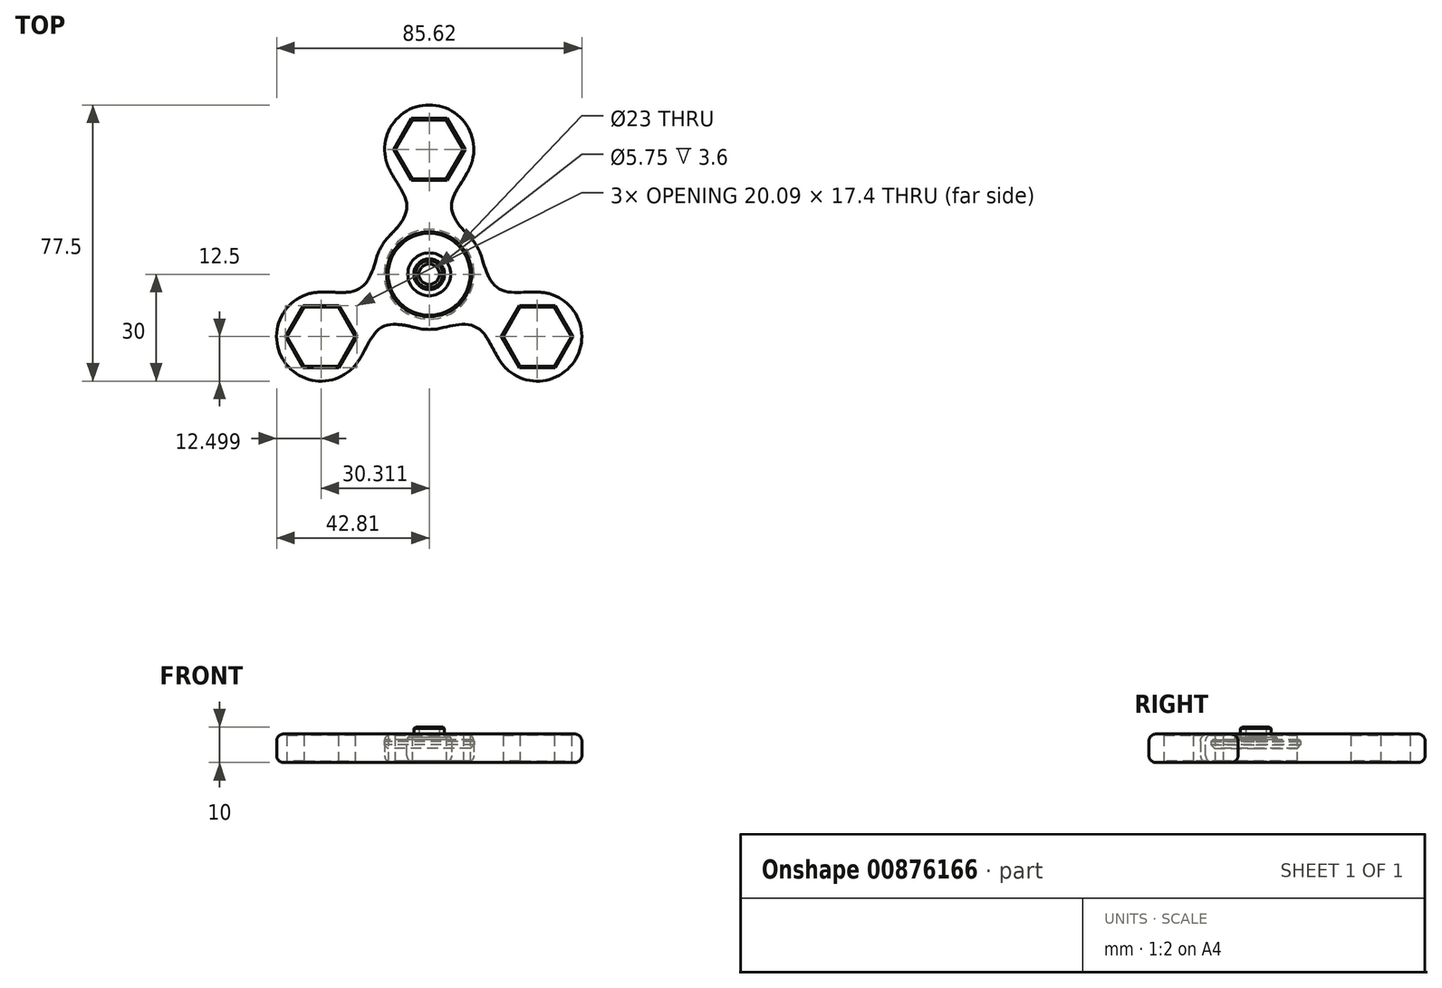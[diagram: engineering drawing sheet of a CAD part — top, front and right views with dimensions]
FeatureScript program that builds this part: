
annotation { "Feature Type Name" : "Feature", "Feature Type Description" : "" }
export const myFeature = defineFeature(function(context is Context, id is Id, definition is map)
    precondition{}
    {
        {
            var Q0;
            Q0=qCreatedBy(makeId("Top.planeOp"),FACE);
            var sketch = newSketch(context, id + "F0", { "sketchPlane" : qUnion([Q0])});
            skCircle(sketch, "E0", {"center": v(0, 0) * mm, "radius": 11.5 * mm});
            skLineSegment(sketch, "E1", {"start": v(0, 0) * mm, "end": v(0, 60.33) * mm, "construction": true});
            skLineSegment(sketch, "E2.1.0", {"start": v(0, 0) * mm, "end": v(-52.24, -30.16) * mm, "construction": true});
            skLineSegment(sketch, "E2.2.0", {"start": v(0, 0) * mm, "end": v(52.24, -30.16) * mm, "construction": true});
            skCircle(sketch, "E3", {"center": v(0, 0) * mm, "radius": 35 * mm, "construction": true});
            skCircle(sketch, "E4", {"center": v(0, 35) * mm, "radius": 12.5 * mm});
            skCircle(sketch, "E5.0", {"center": v(0, 0) * mm, "radius": 15.5 * mm});
            skFitSpline(sketch, "E6", {"points": [v(-12.1, 31.86) * mm, v(-6.42, 20.47) * mm, v(-10.95, 10.97) * mm], "startDerivative": vector(5.97, -22.99) * mm, "endDerivative": vector(-21.64, -21.6) * mm});
            skFitSpline(sketch, "E7.MirrorCS", {"points": [v(12.1, 31.86) * mm, v(6.42, 20.47) * mm, v(10.95, 10.97) * mm], "startDerivative": vector(-5.97, -22.99) * mm, "endDerivative": vector(21.64, -21.6) * mm});
            skCircle(sketch, "E8.cCircle", {"center": v(0, 35) * mm, "radius": 8.3 * mm, "construction": true});
            skLineSegment(sketch, "E8.0", {"start": v(4.8, 26.7) * mm, "end": v(-4.8, 26.7) * mm});
            skLineSegment(sketch, "E8.1", {"start": v(-4.8, 26.7) * mm, "end": v(-9.58, 35) * mm});
            skLineSegment(sketch, "E8.2", {"start": v(-9.58, 35) * mm, "end": v(-4.8, 43.3) * mm});
            skLineSegment(sketch, "E8.3", {"start": v(-4.8, 43.3) * mm, "end": v(4.8, 43.3) * mm});
            skLineSegment(sketch, "E8.4", {"start": v(4.8, 43.3) * mm, "end": v(9.58, 35) * mm});
            skLineSegment(sketch, "E8.5", {"start": v(9.58, 35) * mm, "end": v(4.8, 26.7) * mm});
            skPoint(sketch, "E8.0.midPoint", {"position": v(0, 26.7) * mm});
            skSolve(sketch);
        }
        {
            var Q0;
            Q0=makeQuery(id+"F0.imprint","IMPRINT",FACE,{"disambiguationData":[TD([[makeQuery(id+"F0.imprint","IMPRINT",EDGE,{"derivedFrom":sQuery(id+"F0.wireOp",EDGE,"E8.0")}),1.0]])]});
            var Q1;
            {var subQ0=sQuery(id+"F0.wireOp",EDGE,"E6");var subQ1=sQuery(id+"F0.wireOp",EDGE,"E4");var subQ2=makeQuery(id+"F0.imprint","INTERSECT",VERTEX,{"disambiguationData":[OD(1.0)],"derivedFrom":[subQ1,subQ0]});Q1=makeQuery(id+"F0.imprint","IMPRINT",FACE,{"disambiguationData":[TD([[makeQuery(id+"F0.imprint","IMPRINT",EDGE,{"disambiguationData":[TD([[subQ2,-1.0]])],"derivedFrom":subQ1}),-1.0]])]});}
            extrude(context, id + "F1", {"entities" : qUnion([Q0, Q1]), "endBound" : BoundingType.SYMMETRIC, "depth" : 8 * mm, "offsetDistance" : 25 * mm});
        }
        {
            var Q0;
            Q0=qCreatedBy(makeId("Front.planeOp"),FACE);
            var sketch = newSketch(context, id + "F2", { "sketchPlane" : qUnion([Q0])});
            skLineSegment(sketch, "E9", {"start": v(0, -33.65) * mm, "end": v(0, 33.2) * mm, "construction": true});
            skSolve(sketch);
        }
        {
            var Q0;
            Q0=makeQuery(id+"F1.opExtrude","SWEPT_BODY",BODY,{"disambiguationData":[OSD([sQuery(id+"F0.wireOp",EDGE,"E4"),sQuery(id+"F0.wireOp",EDGE,"E5.0"),sQuery(id+"F0.wireOp",EDGE,"E6"),sQuery(id+"F0.wireOp",EDGE,"E7.MirrorCS"),sQuery(id+"F0.wireOp",EDGE,"E8.0"),sQuery(id+"F0.wireOp",EDGE,"E8.1"),sQuery(id+"F0.wireOp",EDGE,"E8.2"),sQuery(id+"F0.wireOp",EDGE,"E8.3"),sQuery(id+"F0.wireOp",EDGE,"E8.4"),sQuery(id+"F0.wireOp",EDGE,"E8.5")])]});
            var Q1;
            Q1=sQuery(id+"F2.wireOp",EDGE,"E9");
            circularPattern(context, id + "F3", {"entities" : qUnion([Q0]), "axis" : qUnion([Q1]), "angle" : 360 * degree, "instanceCount" : 3, "equalSpace" : true});
        }
        {
            var Q0;
            Q0=makeQuery(id+"F0.imprint","IMPRINT",FACE,{"disambiguationData":[TD([[makeQuery(id+"F0.imprint","IMPRINT",EDGE,{"derivedFrom":sQuery(id+"F0.wireOp",EDGE,"E0")}),-1.0]])]});
            extrude(context, id + "F4", {"entities" : qUnion([Q0]), "endBound" : BoundingType.SYMMETRIC, "depth" : 8 * mm, "offsetDistance" : 25 * mm});
        }
        {
            var Q0;
            Q0=makeQuery(id+"F3.opPattern","COPY",BODY,{"derivedFrom":makeQuery(id+"F1.opExtrude","SWEPT_BODY",BODY,{"disambiguationData":[OSD([sQuery(id+"F0.wireOp",EDGE,"E4"),sQuery(id+"F0.wireOp",EDGE,"E5.0"),sQuery(id+"F0.wireOp",EDGE,"E6"),sQuery(id+"F0.wireOp",EDGE,"E7.MirrorCS"),sQuery(id+"F0.wireOp",EDGE,"E8.0"),sQuery(id+"F0.wireOp",EDGE,"E8.1"),sQuery(id+"F0.wireOp",EDGE,"E8.2"),sQuery(id+"F0.wireOp",EDGE,"E8.3"),sQuery(id+"F0.wireOp",EDGE,"E8.4"),sQuery(id+"F0.wireOp",EDGE,"E8.5")])]}),"instanceName":"1"});
            var Q1;
            Q1=makeQuery(id+"F4.opExtrude","SWEPT_BODY",BODY,{"disambiguationData":[OSD([sQuery(id+"F0.wireOp",EDGE,"E0"),sQuery(id+"F0.wireOp",EDGE,"E5.0")])]});
            var Q2;
            Q2=makeQuery(id+"F3.opPattern","COPY",BODY,{"derivedFrom":makeQuery(id+"F1.opExtrude","SWEPT_BODY",BODY,{"disambiguationData":[OSD([sQuery(id+"F0.wireOp",EDGE,"E4"),sQuery(id+"F0.wireOp",EDGE,"E5.0"),sQuery(id+"F0.wireOp",EDGE,"E6"),sQuery(id+"F0.wireOp",EDGE,"E7.MirrorCS"),sQuery(id+"F0.wireOp",EDGE,"E8.0"),sQuery(id+"F0.wireOp",EDGE,"E8.1"),sQuery(id+"F0.wireOp",EDGE,"E8.2"),sQuery(id+"F0.wireOp",EDGE,"E8.3"),sQuery(id+"F0.wireOp",EDGE,"E8.4"),sQuery(id+"F0.wireOp",EDGE,"E8.5")])]}),"instanceName":"2"});
            var Q3;
            Q3=makeQuery(id+"F1.opExtrude","SWEPT_BODY",BODY,{"disambiguationData":[OSD([sQuery(id+"F0.wireOp",EDGE,"E4"),sQuery(id+"F0.wireOp",EDGE,"E5.0"),sQuery(id+"F0.wireOp",EDGE,"E6"),sQuery(id+"F0.wireOp",EDGE,"E7.MirrorCS"),sQuery(id+"F0.wireOp",EDGE,"E8.0"),sQuery(id+"F0.wireOp",EDGE,"E8.1"),sQuery(id+"F0.wireOp",EDGE,"E8.2"),sQuery(id+"F0.wireOp",EDGE,"E8.3"),sQuery(id+"F0.wireOp",EDGE,"E8.4"),sQuery(id+"F0.wireOp",EDGE,"E8.5")])]});
            booleanBodies(context, id + "F5", {"operationType" : BooleanOperationType.UNION, "tools" : qUnion([Q0, Q1, Q2, Q3])});
        }
        {
            var Q0;
            Q0=makeQuery(id+"F3.opPattern","COPY",EDGE,{"derivedFrom":makeQuery(id+"F1.opExtrude","CAP_EDGE",EDGE,{"disambiguationData":[OSD([sQuery(id+"F0.wireOp",EDGE,"E7.MirrorCS")])],"isStart":true}),"instanceName":"1"});
            var Q1;
            Q1=makeQuery(id+"F3.opPattern","COPY",EDGE,{"derivedFrom":makeQuery(id+"F1.opExtrude","CAP_EDGE",EDGE,{"disambiguationData":[OSD([sQuery(id+"F0.wireOp",EDGE,"E7.MirrorCS")])],"isStart":false}),"instanceName":"1"});
            fillet(context, id + "F6", {"entities" : qUnion([Q0, Q1]), "radius" : 2 * mm, "tangentPropagation" : true, "allowEdgeOverflow" : false});
        }
        {
            var Q0;
            Q0=makeQuery(id+"F4.opExtrude","CAP_EDGE",EDGE,{"disambiguationData":[OSD([sQuery(id+"F0.wireOp",EDGE,"E0")])],"isStart":true});
            var Q1;
            {var subQ0=sQuery(id+"F0.wireOp",EDGE,"E5.0");var subQ1=makeQuery(id+"F1.opExtrude","CAP_FACE",FACE,{"disambiguationData":[OSD([sQuery(id+"F0.wireOp",EDGE,"E4"),subQ0,sQuery(id+"F0.wireOp",EDGE,"E6"),sQuery(id+"F0.wireOp",EDGE,"E7.MirrorCS"),sQuery(id+"F0.wireOp",EDGE,"E8.0"),sQuery(id+"F0.wireOp",EDGE,"E8.1"),sQuery(id+"F0.wireOp",EDGE,"E8.2"),sQuery(id+"F0.wireOp",EDGE,"E8.3"),sQuery(id+"F0.wireOp",EDGE,"E8.4"),sQuery(id+"F0.wireOp",EDGE,"E8.5")])],"isStart":false});Q1=makeQuery(id+"F5.opBoolean","MERGE",FACE,{"derivedFrom":[subQ1,makeQuery(id+"F3.opPattern","COPY",FACE,{"derivedFrom":subQ1,"instanceName":"1"}),makeQuery(id+"F3.opPattern","COPY",FACE,{"derivedFrom":subQ1,"instanceName":"2"}),makeQuery(id+"F4.opExtrude","CAP_FACE",FACE,{"disambiguationData":[OSD([sQuery(id+"F0.wireOp",EDGE,"E0"),subQ0])],"isStart":false})]});}
            chamfer(context, id + "F7", {"entities" : qUnion([Q0, Q1]), "width" : .4 * mm, "tangentPropagation" : true});
        }
        {
            var Q0;
            Q0=makeQuery(id+"F1.opExtrude","CAP_EDGE",EDGE,{"disambiguationData":[OSD([sQuery(id+"F0.wireOp",EDGE,"E8.0")])],"isStart":true});
            var Q1;
            Q1=makeQuery(id+"F1.opExtrude","CAP_EDGE",EDGE,{"disambiguationData":[OSD([sQuery(id+"F0.wireOp",EDGE,"E8.5")])],"isStart":true});
            var Q2;
            Q2=makeQuery(id+"F1.opExtrude","CAP_EDGE",EDGE,{"disambiguationData":[OSD([sQuery(id+"F0.wireOp",EDGE,"E8.4")])],"isStart":true});
            var Q3;
            Q3=makeQuery(id+"F1.opExtrude","CAP_EDGE",EDGE,{"disambiguationData":[OSD([sQuery(id+"F0.wireOp",EDGE,"E8.3")])],"isStart":true});
            var Q4;
            Q4=makeQuery(id+"F1.opExtrude","CAP_EDGE",EDGE,{"disambiguationData":[OSD([sQuery(id+"F0.wireOp",EDGE,"E8.2")])],"isStart":true});
            var Q5;
            Q5=makeQuery(id+"F1.opExtrude","CAP_EDGE",EDGE,{"disambiguationData":[OSD([sQuery(id+"F0.wireOp",EDGE,"E8.1")])],"isStart":true});
            chamfer(context, id + "F8", {"entities" : qUnion([Q0, Q1, Q2, Q3, Q4, Q5]), "width" : .4 * mm, "tangentPropagation" : true});
        }
        {
            var Q0;
            Q0=makeQuery(id+"F3.opPattern","COPY",EDGE,{"derivedFrom":makeQuery(id+"F1.opExtrude","CAP_EDGE",EDGE,{"disambiguationData":[OSD([sQuery(id+"F0.wireOp",EDGE,"E8.0")])],"isStart":true}),"instanceName":"1"});
            var Q1;
            Q1=makeQuery(id+"F3.opPattern","COPY",EDGE,{"derivedFrom":makeQuery(id+"F1.opExtrude","CAP_EDGE",EDGE,{"disambiguationData":[OSD([sQuery(id+"F0.wireOp",EDGE,"E8.1")])],"isStart":true}),"instanceName":"1"});
            var Q2;
            Q2=makeQuery(id+"F3.opPattern","COPY",EDGE,{"derivedFrom":makeQuery(id+"F1.opExtrude","CAP_EDGE",EDGE,{"disambiguationData":[OSD([sQuery(id+"F0.wireOp",EDGE,"E8.2")])],"isStart":true}),"instanceName":"1"});
            var Q3;
            Q3=makeQuery(id+"F3.opPattern","COPY",EDGE,{"derivedFrom":makeQuery(id+"F1.opExtrude","CAP_EDGE",EDGE,{"disambiguationData":[OSD([sQuery(id+"F0.wireOp",EDGE,"E8.3")])],"isStart":true}),"instanceName":"1"});
            var Q4;
            Q4=makeQuery(id+"F3.opPattern","COPY",EDGE,{"derivedFrom":makeQuery(id+"F1.opExtrude","CAP_EDGE",EDGE,{"disambiguationData":[OSD([sQuery(id+"F0.wireOp",EDGE,"E8.4")])],"isStart":true}),"instanceName":"1"});
            var Q5;
            Q5=makeQuery(id+"F3.opPattern","COPY",EDGE,{"derivedFrom":makeQuery(id+"F1.opExtrude","CAP_EDGE",EDGE,{"disambiguationData":[OSD([sQuery(id+"F0.wireOp",EDGE,"E8.5")])],"isStart":true}),"instanceName":"1"});
            var Q6;
            Q6=makeQuery(id+"F3.opPattern","COPY",EDGE,{"derivedFrom":makeQuery(id+"F1.opExtrude","CAP_EDGE",EDGE,{"disambiguationData":[OSD([sQuery(id+"F0.wireOp",EDGE,"E8.4")])],"isStart":true}),"instanceName":"2"});
            var Q7;
            Q7=makeQuery(id+"F3.opPattern","COPY",EDGE,{"derivedFrom":makeQuery(id+"F1.opExtrude","CAP_EDGE",EDGE,{"disambiguationData":[OSD([sQuery(id+"F0.wireOp",EDGE,"E8.3")])],"isStart":true}),"instanceName":"2"});
            var Q8;
            Q8=makeQuery(id+"F3.opPattern","COPY",EDGE,{"derivedFrom":makeQuery(id+"F1.opExtrude","CAP_EDGE",EDGE,{"disambiguationData":[OSD([sQuery(id+"F0.wireOp",EDGE,"E8.2")])],"isStart":true}),"instanceName":"2"});
            var Q9;
            Q9=makeQuery(id+"F3.opPattern","COPY",EDGE,{"derivedFrom":makeQuery(id+"F1.opExtrude","CAP_EDGE",EDGE,{"disambiguationData":[OSD([sQuery(id+"F0.wireOp",EDGE,"E8.1")])],"isStart":true}),"instanceName":"2"});
            var Q10;
            Q10=makeQuery(id+"F3.opPattern","COPY",EDGE,{"derivedFrom":makeQuery(id+"F1.opExtrude","CAP_EDGE",EDGE,{"disambiguationData":[OSD([sQuery(id+"F0.wireOp",EDGE,"E8.0")])],"isStart":true}),"instanceName":"2"});
            var Q11;
            Q11=makeQuery(id+"F3.opPattern","COPY",EDGE,{"derivedFrom":makeQuery(id+"F1.opExtrude","CAP_EDGE",EDGE,{"disambiguationData":[OSD([sQuery(id+"F0.wireOp",EDGE,"E8.5")])],"isStart":true}),"instanceName":"2"});
            chamfer(context, id + "F9", {"entities" : qUnion([Q0, Q1, Q2, Q3, Q4, Q5, Q6, Q7, Q8, Q9, Q10, Q11]), "width" : .4 * mm, "tangentPropagation" : true});
        }
        {
            var Q0;
            Q0=qCreatedBy(makeId("Top.planeOp"),FACE);
            var sketch = newSketch(context, id + "F10", { "sketchPlane" : qUnion([Q0])});
            skCircle(sketch, "E10", {"center": v(0, 0) * mm, "radius": 6 * mm});
            skCircle(sketch, "E11", {"center": v(0, 0) * mm, "radius": 12.61 * mm});
            skCircle(sketch, "E12", {"center": v(0, 0) * mm, "radius": 4.3 * mm});
            skCircle(sketch, "E13", {"center": v(0, 0) * mm, "radius": 2.88 * mm});
            skSolve(sketch);
        }
        {
            var Q0;
            Q0=makeQuery(id+"F10.imprint","IMPRINT",FACE,{"disambiguationData":[TD([[makeQuery(id+"F10.imprint","IMPRINT",EDGE,{"derivedFrom":sQuery(id+"F10.wireOp",EDGE,"E10")}),-1.0]])]});
            var Q1;
            Q1=makeQuery(id+"F10.imprint","IMPRINT",FACE,{"disambiguationData":[TD([[makeQuery(id+"F10.imprint","IMPRINT",EDGE,{"derivedFrom":sQuery(id+"F10.wireOp",EDGE,"E10")}),1.0]])]});
            var Q2;
            Q2=makeQuery(id+"F10.imprint","IMPRINT",FACE,{"disambiguationData":[TD([[makeQuery(id+"F10.imprint","IMPRINT",EDGE,{"derivedFrom":sQuery(id+"F10.wireOp",EDGE,"E12")}),1.0]])]});
            var Q3;
            Q3=makeQuery(id+"F10.imprint","IMPRINT",FACE,{"disambiguationData":[TD([[makeQuery(id+"F10.imprint","IMPRINT",EDGE,{"derivedFrom":sQuery(id+"F10.wireOp",EDGE,"E13")}),1.0]])]});
            extrude(context, id + "F11", {"entities" : qUnion([Q0, Q1, Q2, Q3]), "depth" : 2.4 * mm, "offsetDistance" : 25 * mm});
        }
        {
            var Q0;
            Q0=makeQuery(id+"F10.imprint","IMPRINT",FACE,{"disambiguationData":[TD([[makeQuery(id+"F10.imprint","IMPRINT",EDGE,{"derivedFrom":sQuery(id+"F10.wireOp",EDGE,"E10")}),1.0]])]});
            extrude(context, id + "F12", {"entities" : qUnion([Q0]), "operationType" : NewBodyOperationType.ADD, "depth" : 3 * mm, "offsetDistance" : 25 * mm});
        }
        {
            var Q0;
            Q0=makeQuery(id+"F10.imprint","IMPRINT",FACE,{"disambiguationData":[TD([[makeQuery(id+"F10.imprint","IMPRINT",EDGE,{"derivedFrom":sQuery(id+"F10.wireOp",EDGE,"E12")}),1.0]])]});
            extrude(context, id + "F13", {"entities" : qUnion([Q0]), "operationType" : NewBodyOperationType.ADD, "depth" : 6 * mm, "offsetDistance" : 25 * mm});
        }
        {
            var Q0;
            Q0=makeQuery(id+"F13.opExtrude","CAP_EDGE",EDGE,{"disambiguationData":[OSD([sQuery(id+"F10.wireOp",EDGE,"E12")])],"isStart":false});
            var Q1;
            Q1=makeQuery(id+"F11.opExtrude","CAP_EDGE",EDGE,{"disambiguationData":[OSD([sQuery(id+"F10.wireOp",EDGE,"E11")])],"isStart":false});
            chamfer(context, id + "F14", {"entities" : qUnion([Q0, Q1]), "width" : .5 * mm, "tangentPropagation" : true});
        }
        {
            var Q0;
            Q0=makeQuery(id+"F11.opExtrude","CAP_EDGE",EDGE,{"disambiguationData":[OSD([sQuery(id+"F10.wireOp",EDGE,"E11")])],"isStart":true});
            chamfer(context, id + "F15", {"entities" : qUnion([Q0]), "width" : 1 * mm, "tangentPropagation" : true});
        }
    });
